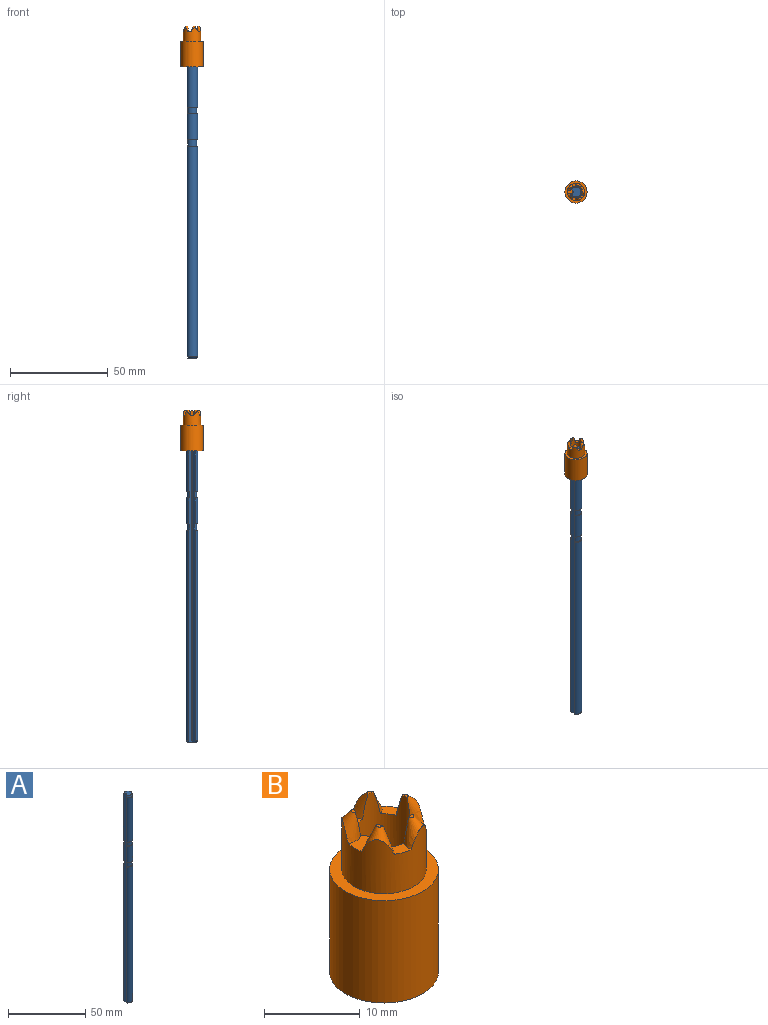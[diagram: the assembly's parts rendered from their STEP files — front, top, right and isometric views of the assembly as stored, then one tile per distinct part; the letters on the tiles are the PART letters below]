
ASSEMBLY  parts=2 mates=1
PART A: 16 faces, bbox 5.6x5.9x165 mm
  f0: cylinder r=2.95mm len=13.2mm, axis (0,0,-1), area 201.2mm2, adj f2,f4,f11,f15
  f1: cylinder r=2.95mm len=107.85mm, axis (0,0,-1), area 1643.7mm2, adj f2,f4,f8,f12
  f2: plane 165.02x1.36mm, normal (-0.71,0.71,0), area 307.8mm2, adj f0,f1,f3,f5,f6,f7,f8,f9
  f3: cylinder r=2.95mm len=35.25mm, axis (0,0,-1), area 537.2mm2, adj f2,f4,f9,f14
  f4: plane 165.02x1.36mm, normal (-0.71,-0.71,0), area 307.8mm2, adj f0,f1,f3,f5,f6,f7,f8,f9
  f5: cylinder r=0.3mm len=165mm, axis (0,0,-1), area 77.8mm2, adj f2,f4,f6,f7
  f6: plane 5.09x4.75mm, normal (0,0,1), area 18.2mm2, adj f2,f4,f5,f9
  f7: plane 4.69x4.41mm, normal (0,0,-1), area 15.6mm2, adj f2,f4,f5,f8
  f8: cone r=2.95mm half-angle=45deg, axis (0,0,1), area 11.7mm2, adj f1,f2,f4,f7
  f9: cone r=2.54mm half-angle=15deg, axis (0,0,-1), area 22.2mm2, adj f2,f3,f4,f6
  f10: cylinder r=2.4mm len=4.8mm, axis (0,0,-1), area 41.8mm2, adj f2,f4,f11,f12
  f11: plane 5.89x5.45mm, normal (0,0,-1), area 7.6mm2, adj f0,f2,f4,f10
  f12: plane 5.89x5.45mm, normal (0,0,1), area 7.6mm2, adj f1,f2,f4,f10
  f13: cylinder r=2.4mm len=4.8mm, axis (0,0,-1), area 41.8mm2, adj f2,f4,f14,f15
  f14: plane 5.89x5.45mm, normal (0,0,-1), area 7.6mm2, adj f2,f3,f4,f13
  f15: plane 5.89x5.45mm, normal (0,0,1), area 7.6mm2, adj f0,f2,f4,f13
PART B: 25 faces, bbox 11.7x11.7x21.3 mm
  f0: cone r=1.8mm half-angle=24.8deg, axis (0.34,0,-0.94), area 9mm2, adj f1,f2,f3,f4,f21
  f1: plane 0.97x0.71mm, normal (0,0,1), area 0.2mm2, adj f0,f2
  f2: cylinder r=3.06mm len=20.85mm, axis (0,0,-1), area 308.4mm2, adj f0,f1,f4,f5,f6,f7,f8,f9
  f3: cylinder r=4.4mm len=8.8mm, axis (0,0,-1), area 159.2mm2, adj f0,f4,f6,f7,f11,f12,f16,f17
  f4: plane 2.32x2.22mm, normal (0,0,1), area 2.2mm2, adj f0,f2,f3,f6
  f5: plane 0.97x0.81mm, normal (0,0,1), area 0.2mm2, adj f2,f6
  f6: cone r=1.8mm half-angle=24.8deg, axis (0.11,0.33,-0.94), area 9mm2, adj f2,f3,f4,f5,f7
  f7: plane 2.2x1.91mm, normal (0,0,1), area 2.2mm2, adj f2,f3,f6,f11
  f8: plane 0.63x0.58mm, normal (0,0,1), area 0.2mm2, adj f2,f11
  f9: cylinder r=0.15mm len=20.77mm, axis (0,0,-1), area 4mm2, adj f2,f10,f11,f23
  f10: plane 20.17x0.68mm, normal (0.71,0.71,0), area 17.7mm2, adj f9,f11,f12,f20,f23
  f11: cone r=1.8mm half-angle=24.8deg, axis (-0.28,0.2,-0.94), area 9.8mm2, adj f2,f3,f7,f8,f9,f10,f12
  f12: plane 2.7x2.17mm, normal (0,0,1), area 4.4mm2, adj f3,f10,f11,f14,f16,f20
  f13: plane 0.63x0.58mm, normal (0,0,1), area 0.2mm2, adj f2,f16
  f14: plane 20.17x0.68mm, normal (0.71,-0.71,0), area 17.7mm2, adj f12,f15,f16,f20,f23
  f15: cylinder r=0.15mm len=20.77mm, axis (0,0,-1), area 4mm2, adj f2,f14,f16,f23
  f16: cone r=1.8mm half-angle=24.8deg, axis (-0.28,-0.2,-0.94), area 9.8mm2, adj f2,f3,f12,f13,f14,f15,f17
  f17: plane 2.2x1.91mm, normal (0,0,1), area 2.2mm2, adj f2,f3,f16,f18
  f18: cone r=1.8mm half-angle=24.8deg, axis (0.11,-0.33,-0.94), area 9mm2, adj f2,f3,f17,f19,f21
  f19: plane 0.97x0.81mm, normal (0,0,1), area 0.2mm2, adj f2,f18
  f20: cylinder r=0.9mm len=17.97mm, axis (0,0,-1), area 25.4mm2, adj f10,f12,f14,f23
  f21: plane 2.32x2.22mm, normal (0,0,1), area 2.2mm2, adj f0,f2,f3,f18
  f22: cylinder r=5.68mm len=13.05mm, axis (0,0,1), area 465.3mm2, adj f23,f24
  f23: plane 11.35x11.35mm, normal (0,0,-1), area 74.2mm2, adj f2,f9,f10,f14,f15,f20,f22
  f24: plane 11.35x11.35mm, normal (0,0,1), area 40.4mm2, adj f3,f22
PLACE A t=(0,0,-162.15)mm
PLACE B at identity fixed
MATE fastened A.f0 <-> B.f2  axis (0,0,1) through (0,0,2.85)mm
